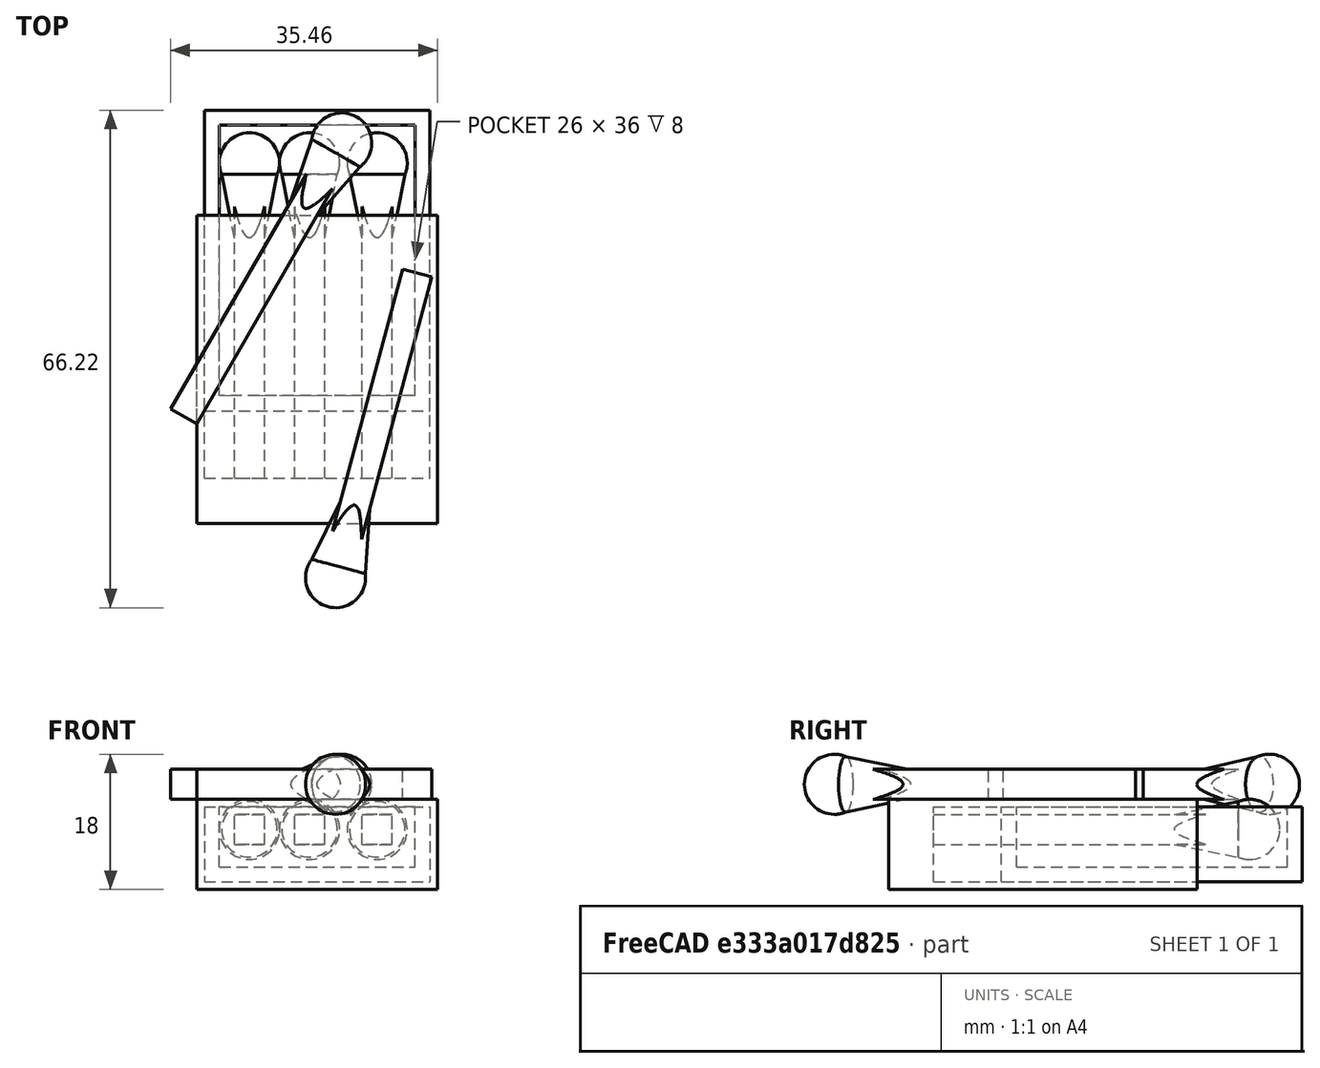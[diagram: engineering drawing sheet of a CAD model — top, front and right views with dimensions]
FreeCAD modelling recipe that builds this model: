
FCSTD DOCUMENT  (FreeCAD 0.18R4 (GitTag))
Label: Спичечный коробок
License: All rights reserved
LicenseURL: http://en.wikipedia.org/wiki/All_rights_reserved
objects: Part::MultiFuse×10, Part::Box×9, Part::Cone×5, Part::Sphere×5, Part::Cut×2
note: 31 computed .brp shape members not serialized (recipe doc carries the construction recipe); baked Part::Feature solids carry a one-line shape summary decoded from their .brp

FEATURE [Part::Box] Box  label="Куб"
  AttacherType = Attacher::AttachEngine3D
  Height = 10
  Length = 30
  Width = 40
FEATURE [Part::Box] Box001  label="Куб001"
  AttacherType = Attacher::AttachEngine3D
  Height = 10
  Length = 26
  Placement = pos=(2,2,2) rot=(0,0,1;0rad)
  Width = 36
FEATURE [Part::Cut] Cut
  Base = -> Box
  Tool = -> Box001
FEATURE [Part::Box] Box002  label="Куб002"
  AttacherType = Attacher::AttachEngine3D
  Height = 12
  Length = 32
  Placement = pos=(-39,-15,0) rot=(0,0,1;0rad)
  Width = 41
FEATURE [Part::Box] Box003  label="Куб003"
  AttacherType = Attacher::AttachEngine3D
  Height = 10
  Length = 30
  Placement = pos=(-38,-9,1) rot=(0,0,1;0rad)
  Width = 37
FEATURE [Part::Cut] Cut001
  Base = -> Box002
  Placement = pos=(38,0,-1) rot=(0,0,1;0rad)
  Tool = -> Box003
FEATURE [Part::Box] Box004  label="Куб004"
  AttacherType = Attacher::AttachEngine3D
  Height = 4
  Length = 4
  Placement = pos=(4,-9,16) rot=(0,0,1;0rad)
  Width = 40
FEATURE [Part::Cone] Cone  label="Конус"
  Angle = 360
  AttacherType = Attacher::AttachEngine3D
  Height = 10
  Placement = pos=(0,0,20) rot=(0,0,1;0rad)
  Radius1 = 2
  Radius2 = 4
FEATURE [Part::Sphere] Sphere  label="Сфера"
  Angle1 = -90
  Angle2 = 90
  Angle3 = 360
  AttacherType = Attacher::AttachEngine3D
  Placement = pos=(0,0,30) rot=(0,0,1;0rad)
  Radius = 4
FEATURE [Part::MultiFuse] Fusion
  Placement = pos=(6,3,18) rot=(1,0,0;4.71239rad)
  Shapes = -> [Sphere,Cone]
FEATURE [Part::MultiFuse] Fusion001
  Placement = pos=(0,0,-11) rot=(0,0,1;0rad)
  Shapes = -> [Box004,Fusion]
FEATURE [Part::Sphere] Sphere001  label="Сфера001"
  Angle1 = -90
  Angle2 = 90
  Angle3 = 360
  AttacherType = Attacher::AttachEngine3D
  Placement = pos=(0,0,30) rot=(0,0,1;0rad)
  Radius = 4
FEATURE [Part::Box] Box005  label="Куб005"
  AttacherType = Attacher::AttachEngine3D
  Height = 4
  Length = 4
  Placement = pos=(4,-9,16) rot=(0,0,1;0rad)
  Width = 40
FEATURE [Part::Cone] Cone001  label="Конус001"
  Angle = 360
  AttacherType = Attacher::AttachEngine3D
  Height = 10
  Placement = pos=(0,0,20) rot=(0,0,1;0rad)
  Radius1 = 2
  Radius2 = 4
FEATURE [Part::MultiFuse] Fusion002
  Placement = pos=(6,3,18) rot=(-1,0,0;1.5708rad)
  Shapes = -> [Sphere001,Cone001]
FEATURE [Part::MultiFuse] Fusion003
  Placement = pos=(8,0,-11) rot=(0,0,1;0rad)
  Shapes = -> [Box005,Fusion002]
FEATURE [Part::Sphere] Sphere002  label="Сфера002"
  Angle1 = -90
  Angle2 = 90
  Angle3 = 360
  AttacherType = Attacher::AttachEngine3D
  Placement = pos=(0,0,30) rot=(0,0,1;0rad)
  Radius = 4
FEATURE [Part::Box] Box006  label="Куб006"
  AttacherType = Attacher::AttachEngine3D
  Height = 4
  Length = 4
  Placement = pos=(4,-9,16) rot=(0,0,1;0rad)
  Width = 40
FEATURE [Part::Cone] Cone002  label="Конус002"
  Angle = 360
  AttacherType = Attacher::AttachEngine3D
  Height = 10
  Placement = pos=(0,0,20) rot=(0,0,1;0rad)
  Radius1 = 2
  Radius2 = 4
FEATURE [Part::MultiFuse] Fusion004
  Placement = pos=(6,3,18) rot=(-1,0,0;1.5708rad)
  Shapes = -> [Sphere002,Cone002]
FEATURE [Part::MultiFuse] Fusion005
  Placement = pos=(17,0,-11) rot=(0,0,1;0rad)
  Shapes = -> [Box006,Fusion004]
FEATURE [Part::Sphere] Sphere003  label="Сфера003"
  Angle1 = -90
  Angle2 = 90
  Angle3 = 360
  AttacherType = Attacher::AttachEngine3D
  Placement = pos=(0,0,30) rot=(0,0,1;0rad)
  Radius = 4
FEATURE [Part::Box] Box007  label="Куб007"
  AttacherType = Attacher::AttachEngine3D
  Height = 4
  Length = 4
  Placement = pos=(4,-9,16) rot=(0,0,1;0rad)
  Width = 40
FEATURE [Part::Cone] Cone003  label="Конус003"
  Angle = 360
  AttacherType = Attacher::AttachEngine3D
  Height = 10
  Placement = pos=(0,0,20) rot=(0,0,1;0rad)
  Radius1 = 2
  Radius2 = 4
FEATURE [Part::MultiFuse] Fusion006
  Placement = pos=(6,3,18) rot=(-1,0,0;1.5708rad)
  Shapes = -> [Sphere003,Cone003]
FEATURE [Part::MultiFuse] Fusion007
  Placement = pos=(-3.4282,10.0622,-5) rot=(0,0,1;5.75959rad)
  Shapes = -> [Box007,Fusion006]
FEATURE [Part::Sphere] Sphere004  label="Сфера004"
  Angle1 = -90
  Angle2 = 90
  Angle3 = 360
  AttacherType = Attacher::AttachEngine3D
  Placement = pos=(0,0,30) rot=(0,0,1;0rad)
  Radius = 4
FEATURE [Part::Cone] Cone004  label="Конус004"
  Angle = 360
  AttacherType = Attacher::AttachEngine3D
  Height = 10
  Placement = pos=(0,0,20) rot=(0,0,1;0rad)
  Radius1 = 2
  Radius2 = 4
FEATURE [Part::MultiFuse] Fusion008
  Placement = pos=(6,3,18) rot=(-1,0,0;1.5708rad)
  Shapes = -> [Sphere004,Cone004]
FEATURE [Part::Box] Box008  label="Куб008"
  AttacherType = Attacher::AttachEngine3D
  Height = 4
  Length = 4
  Placement = pos=(4,-9,16) rot=(0,0,1;0rad)
  Width = 40
FEATURE [Part::MultiFuse] Fusion009
  Placement = pos=(31.7926,8.10634,-5) rot=(0,0,1;2.87979rad)
  Shapes = -> [Fusion008,Box008]
